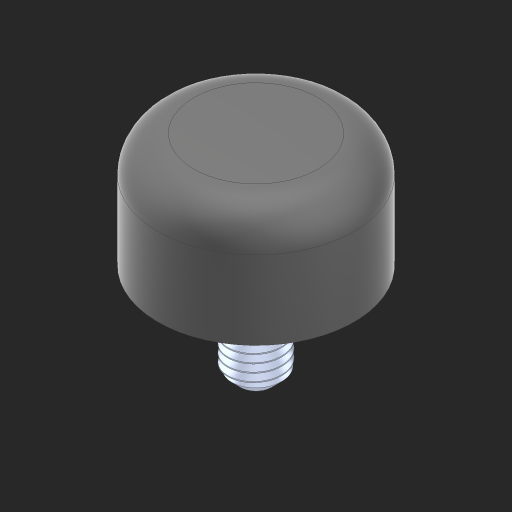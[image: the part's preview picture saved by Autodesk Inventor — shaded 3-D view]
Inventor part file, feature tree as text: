
AUTODESK INVENTOR PART (.ipt)
format: ipt  version: 2023 (Build 270158000, 158)  size: 593,920 bytes
history: native  units: in
note: dims shown in document units (in); Inventor stores cm internally (conversion verified against a paired STEP export)
features: sketch x2, helix x1, revolve x1, chamfer x1, boolean_combine x1
ambient origin geometry x8: Origin, YZ Plane, XZ Plane, XY Plane, X Axis, Y Axis, Z Axis, Center Point
bodies: Solid1 (feature_tree), Solid2 (feature_tree)
feature tree (6):
  helix  "Coil1"  [1 undecoded]
  revolve  "Revolution1"  Angle=30.0deg
  sketch  "Sketch1"  dims[d1=60.0deg d2=30.0deg]
  sketch  "Sketch2"  dims[d3=0.021in d4=0.031in d5=0.5in d6=0.3937in d7=0.0in d8=90.0deg d9=90.0deg d10=0.0in d11=0.0in d12=90.0deg]
  chamfer  "Chamfer1"  Angle=90.0deg  [1 undecoded]
  boolean_combine  "Combine2"
note: 2 required parameter values undecoded (feature->parameter linkage not recoverable at this tier; creation-order binding heuristic only, values carry confidence <= 0.55)
